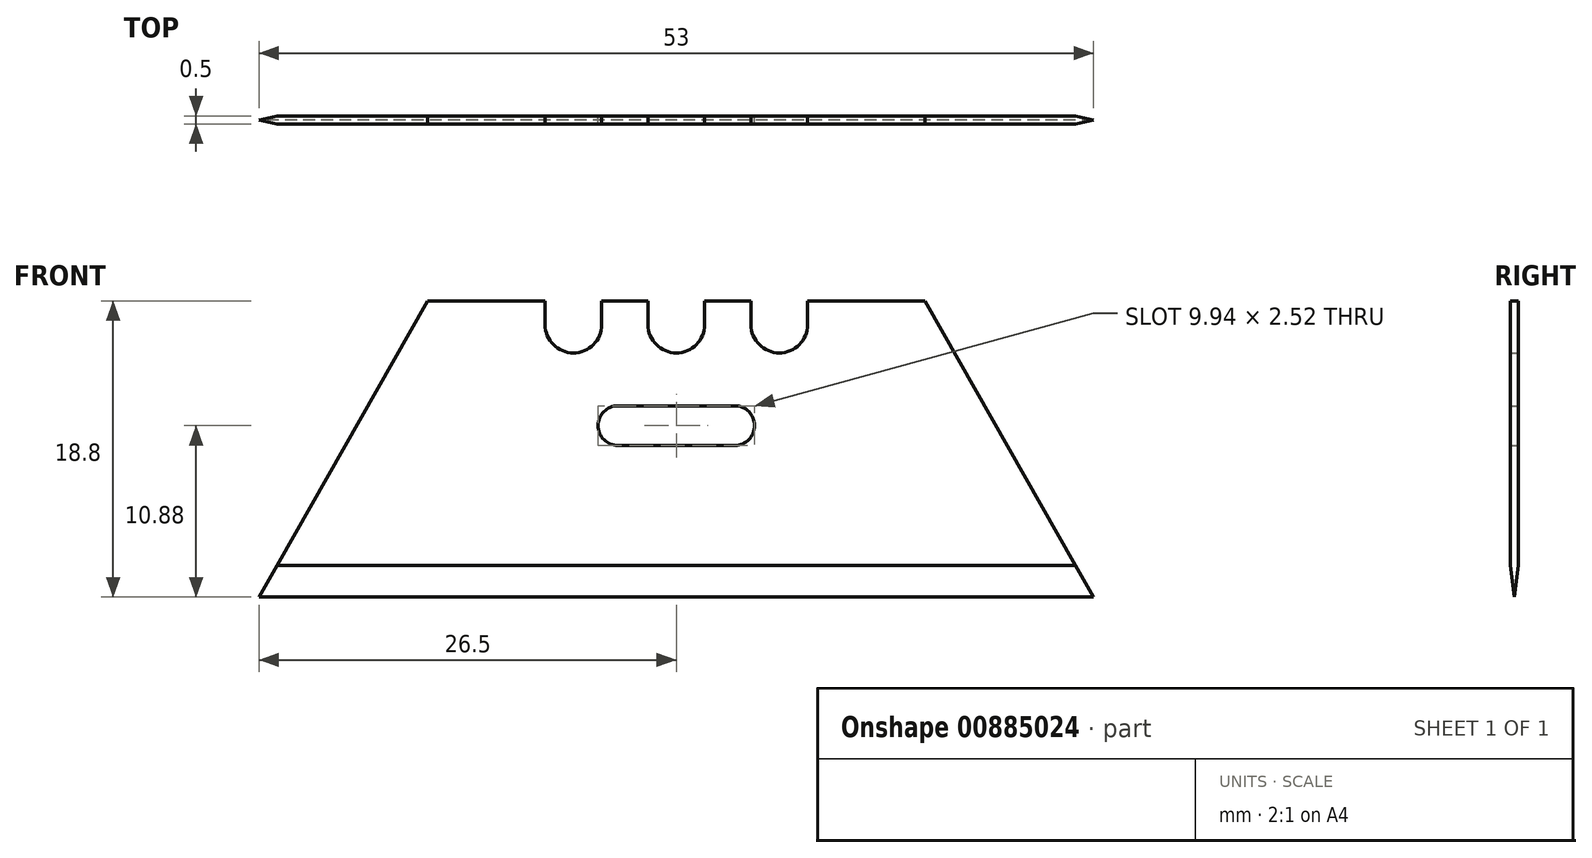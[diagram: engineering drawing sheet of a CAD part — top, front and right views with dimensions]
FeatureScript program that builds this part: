
annotation { "Feature Type Name" : "Feature", "Feature Type Description" : "" }
export const myFeature = defineFeature(function(context is Context, id is Id, definition is map)
    precondition{}
    {
        {
            var Q0;
            Q0=qCreatedBy(makeId("Front.planeOp"),FACE);
            var sketch = newSketch(context, id + "F0", { "sketchPlane" : qUnion([Q0])});
            skLineSegment(sketch, "E0", {"start": v(0, 0) * mm, "end": v(53, 0) * mm});
            skLineSegment(sketch, "E1", {"start": v(53, 0) * mm, "end": v(42.3, 18.8) * mm});
            skLineSegment(sketch, "E2", {"start": v(42.3, 18.8) * mm, "end": v(10.7, 18.8) * mm});
            skLineSegment(sketch, "E3", {"start": v(10.7, 18.8) * mm, "end": v(0, 0) * mm});
            skLineSegment(sketch, "E4", {"start": v(26.5, 18.8) * mm, "end": v(26.5, 0) * mm, "construction": true});
            skLineSegment(sketch, "E5.bottom", {"start": v(22.8, 12.14) * mm, "end": v(30.2, 12.14) * mm});
            skLineSegment(sketch, "E5.top", {"start": v(22.8, 9.62) * mm, "end": v(30.2, 9.62) * mm});
            skLineSegment(sketch, "E5.left", {"start": v(21.53, 10.88) * mm, "end": v(21.53, 10.88) * mm});
            skLineSegment(sketch, "E5.right", {"start": v(31.47, 10.88) * mm, "end": v(31.47, 10.88) * mm});
            skLineSegment(sketch, "E6", {"start": v(26.5, 12.14) * mm, "end": v(26.5, 18.8) * mm, "construction": true});
            skPoint(sketch, "E7.visualSharp", {"position": v(31.47, 12.14) * mm});
            skArc(sketch, "E7.filletArc", {"start": v(31.47, 10.88) * mm, "mid": v(31.1, 11.77) * mm, "end": v(30.2, 12.14) * mm});
            skPoint(sketch, "E8.visualSharp", {"position": v(31.47, 9.62) * mm});
            skArc(sketch, "E8.filletArc", {"start": v(30.2, 9.62) * mm, "mid": v(31.1, 9.99) * mm, "end": v(31.47, 10.88) * mm});
            skPoint(sketch, "E9.visualSharp", {"position": v(21.53, 12.14) * mm});
            skArc(sketch, "E9.filletArc", {"start": v(22.8, 12.14) * mm, "mid": v(21.9, 11.77) * mm, "end": v(21.53, 10.88) * mm});
            skPoint(sketch, "E10.visualSharp", {"position": v(21.53, 9.62) * mm});
            skArc(sketch, "E10.filletArc", {"start": v(21.53, 10.88) * mm, "mid": v(21.9, 9.99) * mm, "end": v(22.8, 9.62) * mm});
            skLineSegment(sketch, "E11.bottom", {"start": v(24.7, 18.8) * mm, "end": v(28.3, 18.8) * mm});
            skLineSegment(sketch, "E11.top", {"start": v(26.5, 15.5) * mm, "end": v(26.5, 15.5) * mm});
            skLineSegment(sketch, "E11.left", {"start": v(24.7, 18.8) * mm, "end": v(24.7, 17.3) * mm});
            skLineSegment(sketch, "E11.right", {"start": v(28.3, 18.8) * mm, "end": v(28.3, 17.3) * mm});
            skPoint(sketch, "E12.visualSharp", {"position": v(24.7, 15.5) * mm});
            skArc(sketch, "E12.filletArc", {"start": v(24.7, 17.3) * mm, "mid": v(25.23, 16.03) * mm, "end": v(26.5, 15.5) * mm});
            skPoint(sketch, "E13.visualSharp", {"position": v(28.3, 15.5) * mm});
            skArc(sketch, "E13.filletArc", {"start": v(26.5, 15.5) * mm, "mid": v(27.77, 16.03) * mm, "end": v(28.3, 17.3) * mm});
            skLineSegment(sketch, "E14", {"start": v(26.5, 18.8) * mm, "end": v(26.5, 12.14) * mm, "construction": true});
            skLineSegment(sketch, "E15.bottom", {"start": v(31.24, 18.8) * mm, "end": v(34.84, 18.8) * mm});
            skLineSegment(sketch, "E15.top", {"start": v(33.04, 15.5) * mm, "end": v(33.04, 15.5) * mm});
            skLineSegment(sketch, "E15.left", {"start": v(31.24, 18.8) * mm, "end": v(31.24, 17.3) * mm});
            skLineSegment(sketch, "E15.right", {"start": v(34.84, 18.8) * mm, "end": v(34.84, 17.3) * mm});
            skLineSegment(sketch, "E16.bottom", {"start": v(18.16, 18.8) * mm, "end": v(21.76, 18.8) * mm});
            skLineSegment(sketch, "E16.top", {"start": v(19.96, 15.5) * mm, "end": v(19.96, 15.5) * mm});
            skLineSegment(sketch, "E16.left", {"start": v(18.16, 18.8) * mm, "end": v(18.16, 17.3) * mm});
            skLineSegment(sketch, "E16.right", {"start": v(21.76, 18.8) * mm, "end": v(21.76, 17.3) * mm});
            skPoint(sketch, "E17.visualSharp", {"position": v(18.16, 15.5) * mm});
            skArc(sketch, "E17.filletArc", {"start": v(18.16, 17.3) * mm, "mid": v(18.69, 16.03) * mm, "end": v(19.96, 15.5) * mm});
            skPoint(sketch, "E18.visualSharp", {"position": v(21.76, 15.5) * mm});
            skArc(sketch, "E18.filletArc", {"start": v(19.96, 15.5) * mm, "mid": v(21.23, 16.03) * mm, "end": v(21.76, 17.3) * mm});
            skPoint(sketch, "E19.visualSharp", {"position": v(31.24, 15.5) * mm});
            skArc(sketch, "E19.filletArc", {"start": v(31.24, 17.3) * mm, "mid": v(31.77, 16.03) * mm, "end": v(33.04, 15.5) * mm});
            skPoint(sketch, "E20.visualSharp", {"position": v(34.84, 15.5) * mm});
            skArc(sketch, "E20.filletArc", {"start": v(33.04, 15.5) * mm, "mid": v(34.31, 16.03) * mm, "end": v(34.84, 17.3) * mm});
            skLineSegment(sketch, "E21", {"start": v(51.86, 2) * mm, "end": v(1.14, 2) * mm, "construction": true});
            skLineSegment(sketch, "E22", {"start": v(51.86, 2) * mm, "end": v(51.86, 0) * mm, "construction": true});
            skSolve(sketch);
        }
        {
            var Q0;
            Q0=makeQuery(id+"F0.imprint","IMPRINT",FACE,{"disambiguationData":[TD([[makeQuery(id+"F0.imprint","IMPRINT",EDGE,{"derivedFrom":sQuery(id+"F0.wireOp",EDGE,"E0")}),1.0]])]});
            extrude(context, id + "F1", {"entities" : qUnion([Q0]), "depth" : 0.5 * mm, "offsetDistance" : 25 * mm});
        }
        {
            var Q0;
            Q0=makeQuery(id+"F1.opExtrude","CAP_FACE",FACE,{"disambiguationData":[OSD([sQuery(id+"F0.wireOp",EDGE,"E0"),sQuery(id+"F0.wireOp",EDGE,"E1"),sQuery(id+"F0.wireOp",EDGE,"E2"),sQuery(id+"F0.wireOp",EDGE,"E3"),sQuery(id+"F0.wireOp",EDGE,"E5.bottom"),sQuery(id+"F0.wireOp",EDGE,"E5.top"),sQuery(id+"F0.wireOp",EDGE,"E7.filletArc"),sQuery(id+"F0.wireOp",EDGE,"E8.filletArc"),sQuery(id+"F0.wireOp",EDGE,"E9.filletArc"),sQuery(id+"F0.wireOp",EDGE,"E10.filletArc"),sQuery(id+"F0.wireOp",EDGE,"E11.left"),sQuery(id+"F0.wireOp",EDGE,"E11.right"),sQuery(id+"F0.wireOp",EDGE,"E12.filletArc"),sQuery(id+"F0.wireOp",EDGE,"E13.filletArc"),sQuery(id+"F0.wireOp",EDGE,"E15.left"),sQuery(id+"F0.wireOp",EDGE,"E15.right"),sQuery(id+"F0.wireOp",EDGE,"E16.left"),sQuery(id+"F0.wireOp",EDGE,"E16.right"),sQuery(id+"F0.wireOp",EDGE,"E17.filletArc"),sQuery(id+"F0.wireOp",EDGE,"E18.filletArc"),sQuery(id+"F0.wireOp",EDGE,"E19.filletArc"),sQuery(id+"F0.wireOp",EDGE,"E20.filletArc")])],"isStart":false});
            var sketch = newSketch(context, id + "F2", { "sketchPlane" : qUnion([Q0])});
            skLineSegment(sketch, "E23.0", {"start": v(51.86, 2) * mm, "end": v(1.14, 2) * mm, "construction": true});
            skLineSegment(sketch, "E23.1", {"start": v(51.86, 2) * mm, "end": v(51.86, 0) * mm, "construction": true});
            skSolve(sketch);
        }
        {
            var Q0;
            Q0=qCreatedBy(makeId("Right.planeOp"),FACE);
            var sketch = newSketch(context, id + "F3", { "sketchPlane" : qUnion([Q0])});
            skPoint(sketch, "E24.0", {"position": v(0, 2) * mm});
            skPoint(sketch, "E24.1", {"position": v(-0.5, 2) * mm});
            skLineSegment(sketch, "E25.0", {"start": v(-0.5, 0) * mm, "end": v(0, 0) * mm});
            skLineSegment(sketch, "E26", {"start": v(0, 2) * mm, "end": v(-0.25, 0) * mm});
            skLineSegment(sketch, "E27", {"start": v(-0.25, 0) * mm, "end": v(-0.5, 2) * mm});
            skLineSegment(sketch, "E28", {"start": v(-0.5, 2) * mm, "end": v(-0.5, 0) * mm});
            skLineSegment(sketch, "E29", {"start": v(0, 2) * mm, "end": v(0, 0) * mm});
            skSolve(sketch);
        }
        {
            var Q0;
            {var subQ2=sQuery(id+"F3.wireOp",EDGE,"E26");Q0=makeQuery(id+"F3.imprint","IMPRINT",FACE,{"disambiguationData":[TD([[makeQuery(id+"F3.imprint","IMPRINT",EDGE,{"derivedFrom":subQ2}),1.0]])]});}
            var Q1;
            {var subQ2=sQuery(id+"F3.wireOp",EDGE,"E27");Q1=makeQuery(id+"F3.imprint","IMPRINT",FACE,{"disambiguationData":[TD([[makeQuery(id+"F3.imprint","IMPRINT",EDGE,{"derivedFrom":subQ2}),1.0]])]});}
            extrude(context, id + "F4", {"entities" : qUnion([Q0, Q1]), "operationType" : NewBodyOperationType.REMOVE, "endBound" : BoundingType.THROUGH_ALL, "depth" : 25 * mm, "offsetDistance" : 25 * mm});
        }
    });
